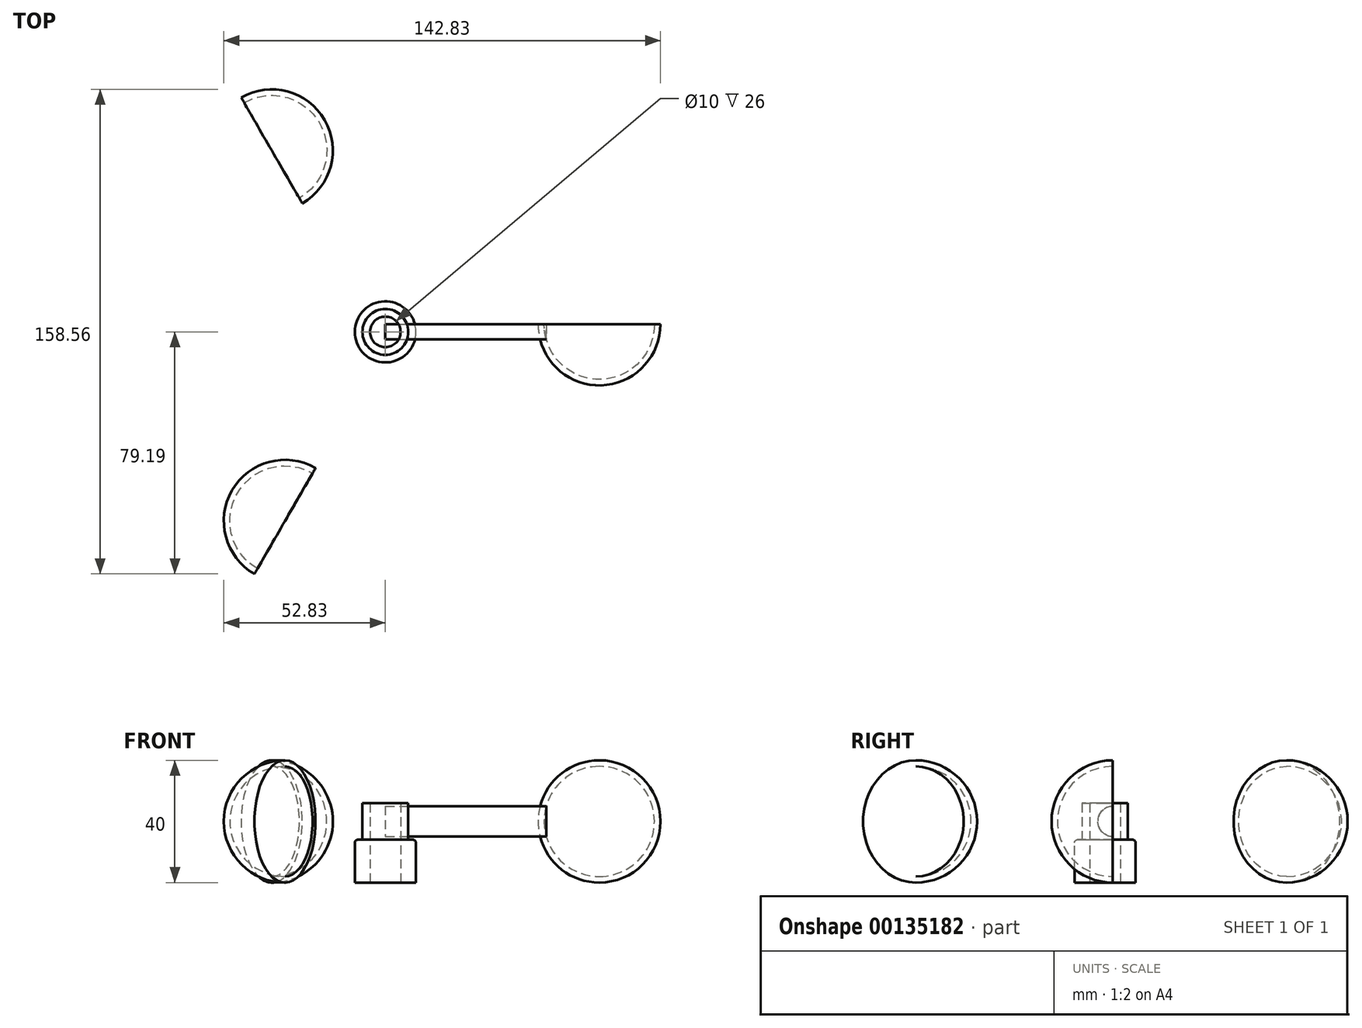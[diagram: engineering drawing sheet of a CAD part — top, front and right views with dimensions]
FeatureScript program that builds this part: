
annotation { "Feature Type Name" : "Feature", "Feature Type Description" : "" }
export const myFeature = defineFeature(function(context is Context, id is Id, definition is map)
    precondition{}
    {
        {
            var Q0;
            Q0=qCreatedBy(makeId("Front.planeOp"),FACE);
            var sketch = newSketch(context, id + "F0", { "sketchPlane" : qUnion([Q0])});
            skArc(sketch, "E0", {"start": v(0, -20) * mm, "mid": v(20, 0) * mm, "end": v(0, 20) * mm});
            skLineSegment(sketch, "E1", {"start": v(0, 20) * mm, "end": v(0, -20) * mm});
            skSolve(sketch);
        }
        {
            var Q0;
            Q0=makeQuery(id+"F0.imprint","IMPRINT",FACE,{"disambiguationData":[TD([[makeQuery(id+"F0.imprint","IMPRINT",EDGE,{"derivedFrom":sQuery(id+"F0.wireOp",EDGE,"E0")}),1.0]])]});
            var Q1;
            Q1=sQuery(id+"F0.wireOp",EDGE,"E1");
            revolve(context, id + "F1", {"entities" : qUnion([Q0]), "axis" : qUnion([Q1]), "revolveType" : RevolveType.ONE_DIRECTION, "angle" : 180 * degree});
        }
        {
            var Q0;
            Q0=qCreatedBy(makeId("Front.planeOp"),FACE);
            var sketch = newSketch(context, id + "F2", { "sketchPlane" : qUnion([Q0])});
            skArc(sketch, "E2", {"start": v(0, -18) * mm, "mid": v(18.05, 0) * mm, "end": v(0, 18) * mm});
            skLineSegment(sketch, "E3", {"start": v(0, 18) * mm, "end": v(0, -18) * mm});
            skSolve(sketch);
        }
        {
            var Q0;
            Q0 = qSketchRegion(id + "F2", true);
            var Q1;
            Q1=sQuery(id+"F2.wireOp",EDGE,"E3");
            revolve(context, id + "F3", {"entities" : qUnion([Q0]), "axis" : qUnion([Q1]), "revolveType" : RevolveType.ONE_DIRECTION, "angle" : 180 * degree});
        }
        {
            var Q0;
            Q0=qCreatedBy(makeId("Right.planeOp"),FACE);
            var sketch = newSketch(context, id + "F4", { "sketchPlane" : qUnion([Q0])});
            skArc(sketch, "E4", {"start": v(0, 5.02) * mm, "mid": v(-4.88, 0.02) * mm, "end": v(0, -4.98) * mm});
            skLineSegment(sketch, "E5", {"start": v(0, 5.02) * mm, "end": v(0, -4.98) * mm});
            skSolve(sketch);
        }
        {
            var Q0;
            Q0 = qSketchRegion(id + "F4", true);
            extrude(context, id + "F5", {"entities" : qUnion([Q0]), "oppositeDirection" : true, "depth" : 70 * mm});
        }
        {
            var Q0;
            Q0=makeQuery(id+"F3.opRevolve","SWEPT_BODY",BODY,{"disambiguationData":[OSD([sQuery(id+"F2.wireOp",EDGE,"E2"),sQuery(id+"F2.wireOp",EDGE,"E3")])]});
            var Q1;
            Q1=makeQuery(id+"F1.opRevolve","SWEPT_BODY",BODY,{"disambiguationData":[OSD([sQuery(id+"F0.wireOp",EDGE,"E0"),sQuery(id+"F0.wireOp",EDGE,"E1")])]});
            var Q2;
            Q2=makeQuery(id+"F5.opExtrude","SWEPT_BODY",BODY,{"disambiguationData":[OSD([sQuery(id+"F4.wireOp",EDGE,"E4"),sQuery(id+"F4.wireOp",EDGE,"E5")])]});
            booleanBodies(context, id + "F6", {"operationType" : BooleanOperationType.SUBTRACTION, "tools" : qUnion([Q0]), "targets" : qUnion([Q1, Q2])});
        }
        {
            var Q0;
            Q0=qCreatedBy(makeId("Front.planeOp"),FACE);
            cPlane(context, id + "F7", {"entities" : qUnion([Q0]), "cplaneType" : CPlaneType.OFFSET, "offset" : 2.5 * mm, "width" : 150 * mm, "height" : 150 * mm});
        }
        {
            var Q0;
            Q0=qCreatedBy(id+"F7.planeOp",FACE);
            var sketch = newSketch(context, id + "F8", { "sketchPlane" : qUnion([Q0])});
            skLineSegment(sketch, "E6", {"start": v(-70, 11.58) * mm, "end": v(-70, -18.87) * mm});
            skSolve(sketch);
        }
        {
            var Q0;
            Q0=qCreatedBy(makeId("Top.planeOp"),FACE);
            var sketch = newSketch(context, id + "F9", { "sketchPlane" : qUnion([Q0])});
            skCircle(sketch, "E7", {"center": v(-70, -2.5) * mm, "radius": 7.5 * mm});
            skSolve(sketch);
        }
        {
            var Q0;
            Q0=makeQuery(id+"F9.imprint","IMPRINT",FACE,{"disambiguationData":[TD([[makeQuery(id+"F9.imprint","IMPRINT",EDGE,{"derivedFrom":sQuery(id+"F9.wireOp",EDGE,"E7")}),1.0]])]});
            extrude(context, id + "F10", {"entities" : qUnion([Q0]), "endBound" : BoundingType.SYMMETRIC, "depth" : 12 * mm});
        }
        {
            var Q0;
            Q0=makeQuery(id+"F10.opExtrude","CAP_FACE",FACE,{"disambiguationData":[OSD([sQuery(id+"F9.wireOp",EDGE,"E7")])],"isStart":true});
            var sketch = newSketch(context, id + "F11", { "sketchPlane" : qUnion([Q0])});
            skCircle(sketch, "E8", {"center": v(-70, 2.5) * mm, "radius": 10 * mm});
            skSolve(sketch);
        }
        {
            var Q0;
            Q0 = qSketchRegion(id + "F11", true);
            extrude(context, id + "F12", {"entities" : qUnion([Q0]), "operationType" : NewBodyOperationType.ADD, "depth" : 14 * mm});
        }
        {
            var Q0;
            Q0=makeQuery(id+"F1.opRevolve","SWEPT_BODY",BODY,{"disambiguationData":[OSD([sQuery(id+"F0.wireOp",EDGE,"E0"),sQuery(id+"F0.wireOp",EDGE,"E1")])]});
            var Q1;
            Q1=sQuery(id+"F8.wireOp",EDGE,"E6");
            transform(context, id + "F13", {"entities" : qUnion([Q0]), "transformType" : TransformType.ROTATION, "transformAxis" : qUnion([Q1]), "angle" : 120 * degree, "makeCopy" : true});
        }
        {
            var Q0;
            Q0=makeQuery(id+"F13.opPattern","COPY",BODY,{"derivedFrom":makeQuery(id+"F1.opRevolve","SWEPT_BODY",BODY,{"disambiguationData":[OSD([sQuery(id+"F0.wireOp",EDGE,"E0"),sQuery(id+"F0.wireOp",EDGE,"E1")])]}),"instanceName":"1"});
            var Q1;
            Q1=sQuery(id+"F8.wireOp",EDGE,"E6");
            transform(context, id + "F14", {"entities" : qUnion([Q0]), "transformType" : TransformType.ROTATION, "transformAxis" : qUnion([Q1]), "angle" : 120 * degree, "makeCopy" : true});
        }
        {
            var Q0;
            Q0=makeQuery(id+"F1.opRevolve","SWEPT_BODY",BODY,{"disambiguationData":[OSD([sQuery(id+"F0.wireOp",EDGE,"E0"),sQuery(id+"F0.wireOp",EDGE,"E1")])]});
            var Q1;
            Q1=makeQuery(id+"F13.opPattern","COPY",BODY,{"derivedFrom":makeQuery(id+"F1.opRevolve","SWEPT_BODY",BODY,{"disambiguationData":[OSD([sQuery(id+"F0.wireOp",EDGE,"E0"),sQuery(id+"F0.wireOp",EDGE,"E1")])]}),"instanceName":"1"});
            var Q2;
            Q2=makeQuery(id+"F14.opPattern","COPY",BODY,{"derivedFrom":makeQuery(id+"F13.opPattern","COPY",BODY,{"derivedFrom":makeQuery(id+"F1.opRevolve","SWEPT_BODY",BODY,{"disambiguationData":[OSD([sQuery(id+"F0.wireOp",EDGE,"E0"),sQuery(id+"F0.wireOp",EDGE,"E1")])]}),"instanceName":"1"}),"instanceName":"1"});
            var Q3;
            Q3=makeQuery(id+"F10.opExtrude","SWEPT_BODY",BODY,{"disambiguationData":[OSD([sQuery(id+"F9.wireOp",EDGE,"E7")])]});
            booleanBodies(context, id + "F15", {"operationType" : BooleanOperationType.SUBTRACTION, "tools" : qUnion([Q0, Q1, Q2]), "targets" : qUnion([Q3]), "offsetAll" : true, "keepTools" : true});
        }
        {
            var Q0;
            Q0=qCreatedBy(makeId("Top.planeOp"),FACE);
            var sketch = newSketch(context, id + "F16", { "sketchPlane" : qUnion([Q0])});
            skCircle(sketch, "E9", {"center": v(-70, -2.5) * mm, "radius": 5 * mm});
            skSolve(sketch);
        }
        {
            var Q0;
            Q0 = qSketchRegion(id + "F16", true);
            extrude(context, id + "F17", {"entities" : qUnion([Q0]), "endBound" : BoundingType.SYMMETRIC, "depth" : 50 * mm});
        }
        {
            var Q0;
            Q0=makeQuery(id+"F17.opExtrude","SWEPT_BODY",BODY,{"disambiguationData":[OSD([sQuery(id+"F16.wireOp",EDGE,"E9")])]});
            var Q1;
            Q1=makeQuery(id+"F1.opRevolve","SWEPT_BODY",BODY,{"disambiguationData":[OSD([sQuery(id+"F0.wireOp",EDGE,"E0"),sQuery(id+"F0.wireOp",EDGE,"E1")])]});
            var Q2;
            Q2=makeQuery(id+"F10.opExtrude","SWEPT_BODY",BODY,{"disambiguationData":[OSD([sQuery(id+"F9.wireOp",EDGE,"E7")])]});
            var Q3;
            Q3=makeQuery(id+"F13.opPattern","COPY",BODY,{"derivedFrom":makeQuery(id+"F1.opRevolve","SWEPT_BODY",BODY,{"disambiguationData":[OSD([sQuery(id+"F0.wireOp",EDGE,"E0"),sQuery(id+"F0.wireOp",EDGE,"E1")])]}),"instanceName":"1"});
            var Q4;
            Q4=makeQuery(id+"F14.opPattern","COPY",BODY,{"derivedFrom":makeQuery(id+"F13.opPattern","COPY",BODY,{"derivedFrom":makeQuery(id+"F1.opRevolve","SWEPT_BODY",BODY,{"disambiguationData":[OSD([sQuery(id+"F0.wireOp",EDGE,"E0"),sQuery(id+"F0.wireOp",EDGE,"E1")])]}),"instanceName":"1"}),"instanceName":"1"});
            booleanBodies(context, id + "F18", {"operationType" : BooleanOperationType.SUBTRACTION, "tools" : qUnion([Q0]), "targets" : qUnion([Q1, Q2, Q3, Q4])});
        }
        {
            var Q0;
            Q0=makeQuery(id+"F10.opExtrude","CAP_EDGE",EDGE,{"disambiguationData":[OSD([sQuery(id+"F9.wireOp",EDGE,"E7")])],"isStart":true});
            var Q1;
            Q1=makeQuery(id+"F12.opExtrude","CAP_EDGE",EDGE,{"disambiguationData":[OSD([sQuery(id+"F11.wireOp",EDGE,"E8")])],"isStart":true});
            fillet(context, id + "F19", {"entities" : qUnion([Q0, Q1]), "radius" : 1 * mm, "tangentPropagation" : true, "allowEdgeOverflow" : false});
        }
    });
